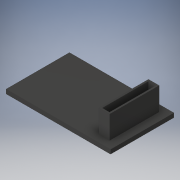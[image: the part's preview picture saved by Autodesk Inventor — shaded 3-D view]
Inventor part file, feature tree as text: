
AUTODESK INVENTOR PART (.ipt)
format: ipt  version: 2019 (Build 230136000, 136)  size: 130,048 bytes
history: native  units: mm
features: extrude x2, sketch x2
ambient origin geometry x8: Origin, YZ Plane, XZ Plane, XY Plane, X Axis, Y Axis, Z Axis, Center Point
bodies: Solid1 (feature_tree)
feature tree (4):
  extrude  "Extrusion1"  Depth=60.0mm
  extrude  "Extrusion2"  Depth=44.0mm
  sketch  "Sketch1"  dims[d0=99.0mm d1=60.0mm]
  sketch  "Sketch2"  dims[d2=7.0mm d3=44.0mm d4=8.0mm d5=9.0mm d6=4.0mm d7=0.0mm d8=1.5mm d9=22.0mm d10=0.0mm]
